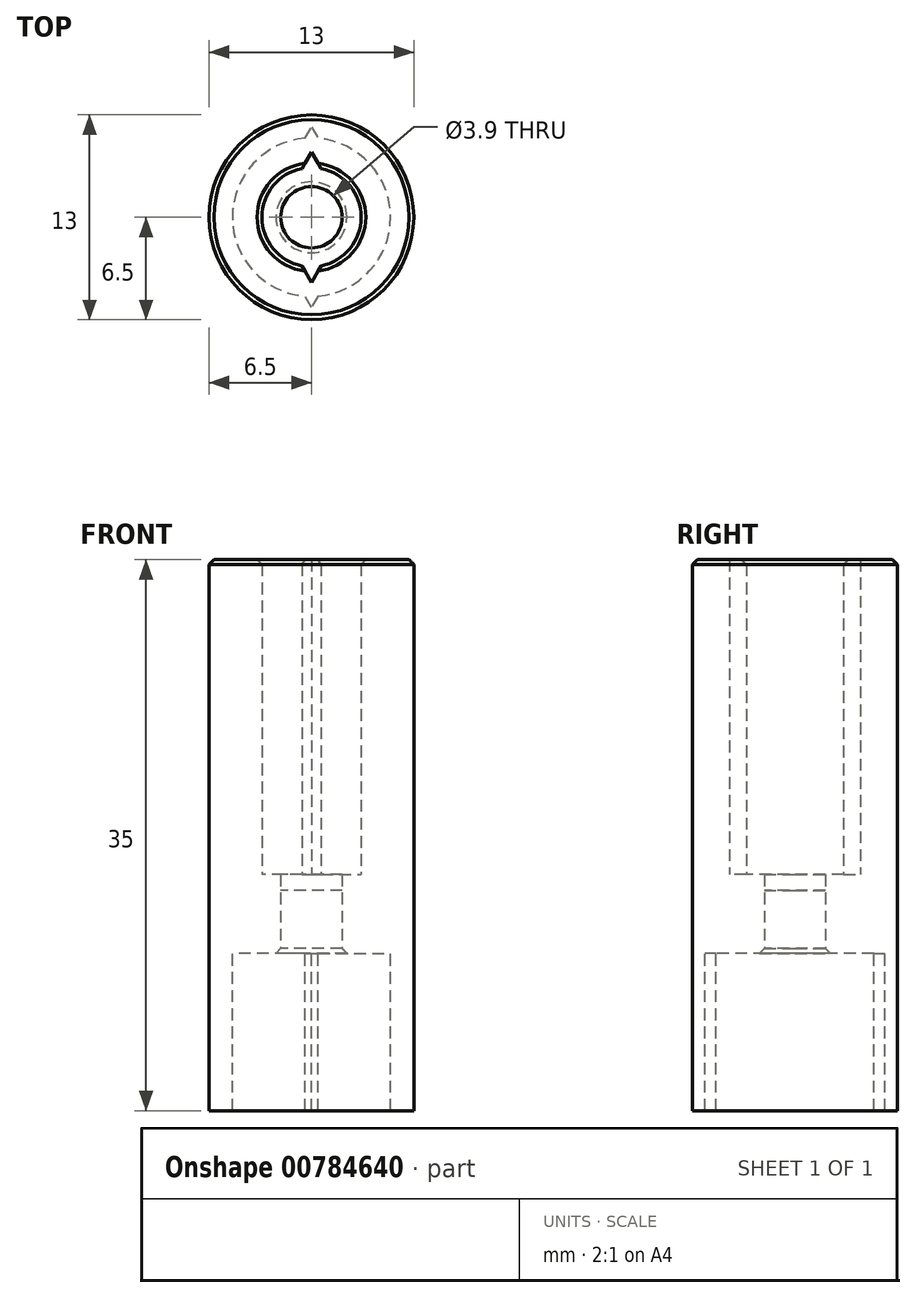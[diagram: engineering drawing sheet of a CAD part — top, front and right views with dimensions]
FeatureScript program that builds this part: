
annotation { "Feature Type Name" : "Feature", "Feature Type Description" : "" }
export const myFeature = defineFeature(function(context is Context, id is Id, definition is map)
    precondition{}
    {
        {
            var Q0;
            Q0=qCreatedBy(makeId("Top.planeOp"),FACE);
            var sketch = newSketch(context, id + "F0", { "sketchPlane" : qUnion([Q0])});
            skCircle(sketch, "E0", {"center": v(0, 0) * mm, "radius": 3.15 * mm});
            skCircle(sketch, "E1", {"center": v(0, 0) * mm, "radius": 1.95 * mm});
            skCircle(sketch, "E2", {"center": v(0, 0) * mm, "radius": 5.03 * mm});
            skCircle(sketch, "E3", {"center": v(0, 0) * mm, "radius": 6.5 * mm});
            skCircle(sketch, "E4.cCircle", {"center": v(0, 3.15) * mm, "radius": 0.5 * mm, "construction": true});
            skLineSegment(sketch, "E4.0", {"start": v(0.87, 2.65) * mm, "end": v(-0.87, 2.65) * mm});
            skLineSegment(sketch, "E4.1", {"start": v(-0.87, 2.65) * mm, "end": v(0, 4.15) * mm});
            skLineSegment(sketch, "E4.2", {"start": v(0, 4.15) * mm, "end": v(0.87, 2.65) * mm});
            skPoint(sketch, "E4.0.midPoint", {"position": v(0, 2.65) * mm});
            skCircle(sketch, "E5.cCircle", {"center": v(0, 5.03) * mm, "radius": 0.35 * mm, "construction": true});
            skLineSegment(sketch, "E5.0", {"start": v(0.6, 4.68) * mm, "end": v(-0.6, 4.68) * mm});
            skLineSegment(sketch, "E5.1", {"start": v(-0.6, 4.68) * mm, "end": v(0, 5.73) * mm});
            skLineSegment(sketch, "E5.2", {"start": v(0, 5.73) * mm, "end": v(0.6, 4.68) * mm});
            skPoint(sketch, "E5.0.midPoint", {"position": v(0, 4.68) * mm});
            skCircle(sketch, "E6.cCircle", {"center": v(0, -3.15) * mm, "radius": 0.5 * mm, "construction": true});
            skLineSegment(sketch, "E6.0", {"start": v(-0.87, -2.65) * mm, "end": v(0.87, -2.65) * mm});
            skLineSegment(sketch, "E6.1", {"start": v(0.87, -2.65) * mm, "end": v(0, -4.15) * mm});
            skLineSegment(sketch, "E6.2", {"start": v(0, -4.15) * mm, "end": v(-0.87, -2.65) * mm});
            skPoint(sketch, "E6.0.midPoint", {"position": v(0, -2.65) * mm});
            skCircle(sketch, "E7.cCircle", {"center": v(0, -5.03) * mm, "radius": 0.35 * mm, "construction": true});
            skLineSegment(sketch, "E7.0", {"start": v(-0.6, -4.68) * mm, "end": v(0.6, -4.68) * mm});
            skLineSegment(sketch, "E7.1", {"start": v(0.6, -4.68) * mm, "end": v(0, -5.72) * mm});
            skLineSegment(sketch, "E7.2", {"start": v(0, -5.73) * mm, "end": v(-0.6, -4.68) * mm});
            skPoint(sketch, "E7.0.midPoint", {"position": v(0, -4.68) * mm});
            skSolve(sketch);
        }
        {
            var Q0;
            Q0=makeQuery(id+"F0.imprint","IMPRINT",FACE,{"disambiguationData":[TD([[makeQuery(id+"F0.imprint","IMPRINT",EDGE,{"derivedFrom":sQuery(id+"F0.wireOp",EDGE,"IpKKJteX-Mf2E-EgKo-yrXk-ianrxKYjUgDh")}),-1.0]])]});
            var Q1;
            Q1=makeQuery(id+"F0.imprint","IMPRINT",FACE,{"disambiguationData":[TD([[makeQuery(id+"F0.imprint","IMPRINT",EDGE,{"derivedFrom":sQuery(id+"F0.wireOp",EDGE,"E2")}),-1.0]])]});
            var Q2;
            Q2=makeQuery(id+"F0.imprint","IMPRINT",FACE,{"disambiguationData":[TD([[makeQuery(id+"F0.imprint","IMPRINT",EDGE,{"derivedFrom":sQuery(id+"F0.wireOp",EDGE,"IpKKJteX-Mf2E-EgKo-yrXk-ianrxKYjUgDh")}),1.0]])]});
            var Q3;
            Q3=makeQuery(id+"F0.imprint","IMPRINT",FACE,{"disambiguationData":[TD([[makeQuery(id+"F0.imprint","IMPRINT",EDGE,{"derivedFrom":sQuery(id+"F0.wireOp",EDGE,"E3")}),1.0]])]});
            var Q4;
            {var subQ5=sQuery(id+"F0.wireOp",EDGE,"E7.0");Q4=makeQuery(id+"F0.imprint","IMPRINT",FACE,{"disambiguationData":[TD([[makeQuery(id+"F0.imprint","IMPRINT",EDGE,{"derivedFrom":subQ5}),-1.0]])]});}
            var Q5;
            {var subQ0=sQuery(id+"F0.wireOp",EDGE,"E7.2");var subQ1=sQuery(id+"F0.wireOp",EDGE,"E2");var subQ2=makeQuery(id+"F0.imprint","INTERSECT",VERTEX,{"derivedFrom":[subQ1,subQ0]});Q5=makeQuery(id+"F0.imprint","IMPRINT",FACE,{"disambiguationData":[TD([[makeQuery(id+"F0.imprint","IMPRINT",EDGE,{"disambiguationData":[TD([[subQ2,-1.0]])],"derivedFrom":subQ1}),-1.0]])]});}
            var Q6;
            {var subQ0=sQuery(id+"F0.wireOp",EDGE,"E5.1");var subQ1=sQuery(id+"F0.wireOp",EDGE,"E2");var subQ2=makeQuery(id+"F0.imprint","INTERSECT",VERTEX,{"derivedFrom":[subQ1,subQ0]});Q6=makeQuery(id+"F0.imprint","IMPRINT",FACE,{"disambiguationData":[TD([[makeQuery(id+"F0.imprint","IMPRINT",EDGE,{"disambiguationData":[TD([[subQ2,1.0]])],"derivedFrom":subQ1}),-1.0]])]});}
            var Q7;
            {var subQ5=sQuery(id+"F0.wireOp",EDGE,"E5.0");Q7=makeQuery(id+"F0.imprint","IMPRINT",FACE,{"disambiguationData":[TD([[makeQuery(id+"F0.imprint","IMPRINT",EDGE,{"derivedFrom":subQ5}),-1.0]])]});}
            var Q8;
            {var subQ6=sQuery(id+"F0.wireOp",EDGE,"E5.0");Q8=makeQuery(id+"F0.imprint","IMPRINT",FACE,{"disambiguationData":[TD([[makeQuery(id+"F0.imprint","IMPRINT",EDGE,{"derivedFrom":subQ6}),1.0]])]});}
            extrude(context, id + "F1", {"entities" : qUnion([Q0, Q1, Q2, Q3, Q4, Q5, Q6, Q7, Q8]), "depth" : 25 * mm, "offsetDistance" : 25 * mm});
        }
        {
            var Q0;
            Q0=makeQuery(id+"F0.imprint","IMPRINT",FACE,{"disambiguationData":[TD([[makeQuery(id+"F0.imprint","IMPRINT",EDGE,{"derivedFrom":sQuery(id+"F0.wireOp",EDGE,"E0")}),1.0]])]});
            var Q1;
            Q1=makeQuery(id+"F0.imprint","IMPRINT",FACE,{"disambiguationData":[TD([[makeQuery(id+"F0.imprint","IMPRINT",EDGE,{"derivedFrom":sQuery(id+"F0.wireOp",EDGE,"IpKKJteX-Mf2E-EgKo-yrXk-ianrxKYjUgDh")}),-1.0]])]});
            var Q2;
            Q2=makeQuery(id+"F0.imprint","IMPRINT",FACE,{"disambiguationData":[TD([[makeQuery(id+"F0.imprint","IMPRINT",EDGE,{"derivedFrom":sQuery(id+"F0.wireOp",EDGE,"E2")}),-1.0]])]});
            var Q3;
            Q3=makeQuery(id+"F0.imprint","IMPRINT",FACE,{"disambiguationData":[TD([[makeQuery(id+"F0.imprint","IMPRINT",EDGE,{"derivedFrom":sQuery(id+"F0.wireOp",EDGE,"E1")}),-1.0]])]});
            var Q4;
            Q4=makeQuery(id+"F0.imprint","IMPRINT",FACE,{"disambiguationData":[TD([[makeQuery(id+"F0.imprint","IMPRINT",EDGE,{"derivedFrom":sQuery(id+"F0.wireOp",EDGE,"E3")}),1.0]])]});
            var Q5;
            Q5=makeQuery(id+"F1.opExtrude","CAP_FACE",FACE,{"disambiguationData":[OSD([sQuery(id+"F0.wireOp",EDGE,"E2"),sQuery(id+"F0.wireOp",EDGE,"E5.1"),sQuery(id+"F0.wireOp",EDGE,"E5.2")])],"isStart":false});
            var Q6;
            Q6=makeQuery(id+"F0.imprint","IMPRINT",FACE,{"disambiguationData":[TD([[makeQuery(id+"F0.imprint","IMPRINT",EDGE,{"derivedFrom":sQuery(id+"F0.wireOp",EDGE,"IpKKJteX-Mf2E-EgKo-yrXk-ianrxKYjUgDh")}),1.0]])]});
            var Q7;
            {var subQ0=sQuery(id+"F0.wireOp",EDGE,"E6.2");var subQ1=sQuery(id+"F0.wireOp",EDGE,"E0");var subQ2=makeQuery(id+"F0.imprint","INTERSECT",VERTEX,{"derivedFrom":[subQ1,subQ0]});Q7=makeQuery(id+"F0.imprint","IMPRINT",FACE,{"disambiguationData":[TD([[makeQuery(id+"F0.imprint","IMPRINT",EDGE,{"disambiguationData":[TD([[subQ2,-1.0]])],"derivedFrom":subQ1}),-1.0]])]});}
            var Q8;
            {var subQ5=sQuery(id+"F0.wireOp",EDGE,"E6.0");Q8=makeQuery(id+"F0.imprint","IMPRINT",FACE,{"disambiguationData":[TD([[makeQuery(id+"F0.imprint","IMPRINT",EDGE,{"derivedFrom":subQ5}),-1.0]])]});}
            var Q9;
            {var subQ5=sQuery(id+"F0.wireOp",EDGE,"E4.0");Q9=makeQuery(id+"F0.imprint","IMPRINT",FACE,{"disambiguationData":[TD([[makeQuery(id+"F0.imprint","IMPRINT",EDGE,{"derivedFrom":subQ5}),-1.0]])]});}
            var Q10;
            {var subQ0=sQuery(id+"F0.wireOp",EDGE,"E4.1");var subQ1=sQuery(id+"F0.wireOp",EDGE,"E0");var subQ2=makeQuery(id+"F0.imprint","INTERSECT",VERTEX,{"derivedFrom":[subQ1,subQ0]});Q10=makeQuery(id+"F0.imprint","IMPRINT",FACE,{"disambiguationData":[TD([[makeQuery(id+"F0.imprint","IMPRINT",EDGE,{"disambiguationData":[TD([[subQ2,1.0]])],"derivedFrom":subQ1}),-1.0]])]});}
            var Q11;
            {var subQ0=sQuery(id+"F0.wireOp",EDGE,"E5.1");var subQ1=sQuery(id+"F0.wireOp",EDGE,"E2");var subQ2=makeQuery(id+"F0.imprint","INTERSECT",VERTEX,{"derivedFrom":[subQ1,subQ0]});Q11=makeQuery(id+"F0.imprint","IMPRINT",FACE,{"disambiguationData":[TD([[makeQuery(id+"F0.imprint","IMPRINT",EDGE,{"disambiguationData":[TD([[subQ2,1.0]])],"derivedFrom":subQ1}),-1.0]])]});}
            var Q12;
            {var subQ5=sQuery(id+"F0.wireOp",EDGE,"E7.0");Q12=makeQuery(id+"F0.imprint","IMPRINT",FACE,{"disambiguationData":[TD([[makeQuery(id+"F0.imprint","IMPRINT",EDGE,{"derivedFrom":subQ5}),-1.0]])]});}
            var Q13;
            {var subQ0=sQuery(id+"F0.wireOp",EDGE,"E7.2");var subQ1=sQuery(id+"F0.wireOp",EDGE,"E2");var subQ2=makeQuery(id+"F0.imprint","INTERSECT",VERTEX,{"derivedFrom":[subQ1,subQ0]});Q13=makeQuery(id+"F0.imprint","IMPRINT",FACE,{"disambiguationData":[TD([[makeQuery(id+"F0.imprint","IMPRINT",EDGE,{"disambiguationData":[TD([[subQ2,-1.0]])],"derivedFrom":subQ1}),-1.0]])]});}
            var Q14;
            {var subQ5=sQuery(id+"F0.wireOp",EDGE,"E5.0");Q14=makeQuery(id+"F0.imprint","IMPRINT",FACE,{"disambiguationData":[TD([[makeQuery(id+"F0.imprint","IMPRINT",EDGE,{"derivedFrom":subQ5}),-1.0]])]});}
            extrude(context, id + "F2", {"entities" : qUnion([Q0, Q1, Q2, Q3, Q4, Q5, Q6, Q7, Q8, Q9, Q10, Q11, Q12, Q13, Q14]), "operationType" : NewBodyOperationType.ADD, "depth" : 5 * mm, "offsetDistance" : 25 * mm});
        }
        {
            var Q0;
            Q0=makeQuery(id+"F0.imprint","IMPRINT",FACE,{"disambiguationData":[TD([[makeQuery(id+"F0.imprint","IMPRINT",EDGE,{"derivedFrom":sQuery(id+"F0.wireOp",EDGE,"E3")}),1.0]])]});
            extrude(context, id + "F3", {"entities" : qUnion([Q0]), "operationType" : NewBodyOperationType.ADD, "oppositeDirection" : true, "depth" : 10 * mm, "offsetDistance" : 25 * mm});
        }
        {
            var Q0;
            Q0=makeQuery(id+"F1.opExtrude","CAP_EDGE",EDGE,{"disambiguationData":[OSD([sQuery(id+"F0.wireOp",EDGE,"E3")])],"isStart":false});
            var Q1;
            Q1=makeQuery(id+"F1.opExtrude","CAP_EDGE",EDGE,{"disambiguationData":[OSD([sQuery(id+"F0.wireOp",EDGE,"E0")])],"isStart":false});
            var Q2;
            Q2=makeQuery(id+"F2.opExtrude","CAP_EDGE",EDGE,{"disambiguationData":[OSD([sQuery(id+"F0.wireOp",EDGE,"E1")])],"isStart":true});
            chamfer(context, id + "F4", {"entities" : qUnion([Q0, Q1, Q2]), "width" : 0.3 * mm, "tangentPropagation" : true});
        }
        {
            var Q0;
            Q0=makeQuery(id+"F0.imprint","IMPRINT",FACE,{"disambiguationData":[TD([[makeQuery(id+"F0.imprint","IMPRINT",EDGE,{"derivedFrom":sQuery(id+"F0.wireOp",EDGE,"E1")}),1.0]])]});
            var Q1;
            Q1=makeQuery(id+"F2.opExtrude","CAP_FACE",FACE,{"disambiguationData":[OSD([sQuery(id+"F0.wireOp",EDGE,"E0"),sQuery(id+"F0.wireOp",EDGE,"E1"),sQuery(id+"F0.wireOp",EDGE,"E4.1"),sQuery(id+"F0.wireOp",EDGE,"E4.2")])],"isStart":false});
            var Q2;
            Q2=makeQuery(id+"F2.opExtrude","CAP_FACE",FACE,{"disambiguationData":[OSD([sQuery(id+"F0.wireOp",EDGE,"E0"),sQuery(id+"F0.wireOp",EDGE,"E1"),sQuery(id+"F0.wireOp",EDGE,"E4.1"),sQuery(id+"F0.wireOp",EDGE,"E4.2")])],"isStart":false});
            extrude(context, id + "F5", {"entities" : qUnion([Q0]), "endBound" : BoundingType.UP_TO_SURFACE, "depth" : 25 * mm, "endBoundEntityFace" : qUnion([Q1]), "offsetDistance" : 25 * mm, "hasSecondDirection" : true, "secondDirectionBound" : BoundingType.UP_TO_SURFACE, "secondDirectionOppositeDirection" : false, "secondDirectionDepth" : 25 * mm, "secondDirectionBoundEntityFace" : qUnion([Q2]), "hasSecondDirectionOffset" : true, "secondDirectionOffsetDistance" : 1 * mm});
        }
    });
